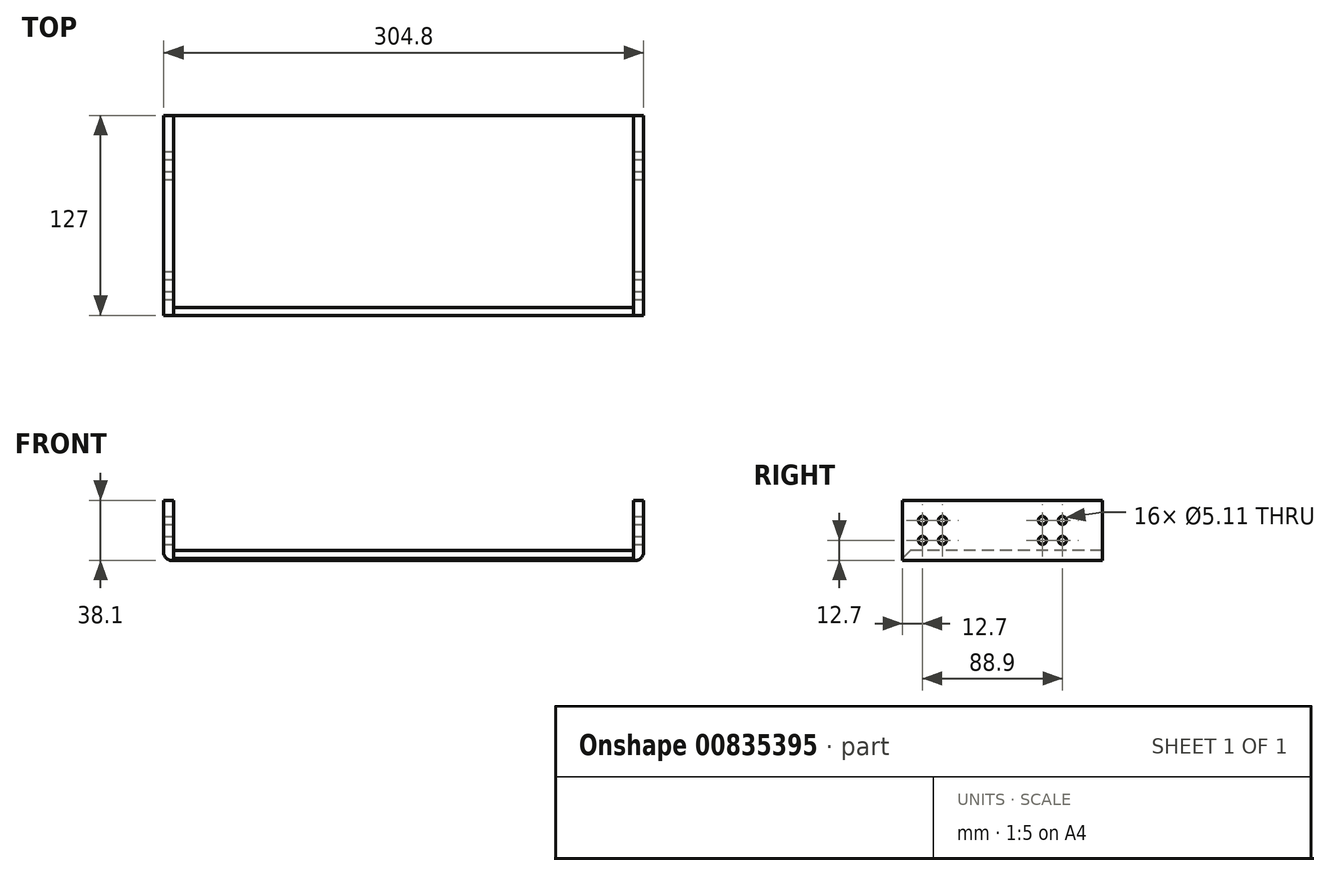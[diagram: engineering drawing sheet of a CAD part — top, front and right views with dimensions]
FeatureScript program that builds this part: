
annotation { "Feature Type Name" : "Feature", "Feature Type Description" : "" }
export const myFeature = defineFeature(function(context is Context, id is Id, definition is map)
    precondition{}
    {
        {
            var Q0;
            Q0=qCreatedBy(makeId("Front.planeOp"),FACE);
            var sketch = newSketch(context, id + "F0", { "sketchPlane" : qUnion([Q0])});
            skLineSegment(sketch, "E0.bottom", {"start": v(0, 0) * mm, "end": v(-304.8, 0) * mm});
            skLineSegment(sketch, "E0.top", {"start": v(0, 38.1) * mm, "end": v(-6.35, 38.1) * mm});
            skLineSegment(sketch, "E0.left", {"start": v(0, 0) * mm, "end": v(0, 38.1) * mm});
            skLineSegment(sketch, "E0.right", {"start": v(-304.8, 0) * mm, "end": v(-304.8, 38.1) * mm});
            skLineSegment(sketch, "E1.top", {"start": v(-304.8, 38.1) * mm, "end": v(-298.45, 38.1) * mm});
            skLineSegment(sketch, "E1.right", {"start": v(-298.45, 6.35) * mm, "end": v(-298.45, 38.1) * mm});
            skLineSegment(sketch, "E2.top", {"start": v(-298.45, 6.35) * mm, "end": v(-6.35, 6.35) * mm});
            skLineSegment(sketch, "E2.left", {"start": v(-298.45, 38.1) * mm, "end": v(-298.45, 6.35) * mm});
            skLineSegment(sketch, "E2.right", {"start": v(-6.35, 38.1) * mm, "end": v(-6.35, 6.35) * mm});
            skSolve(sketch);
        }
        {
            var Q0;
            Q0=makeQuery(id+"F0.imprint","IMPRINT",FACE,{"disambiguationData":[TD([[makeQuery(id+"F0.imprint","IMPRINT",EDGE,{"derivedFrom":sQuery(id+"F0.wireOp",EDGE,"E0.bottom")}),-1.0]])]});
            extrude(context, id + "F1", {"entities" : qUnion([Q0]), "oppositeDirection" : true, "depth" : 127 * mm, "offsetDistance" : 25.4 * mm});
        }
        {
            var Q0;
            Q0=makeQuery(id+"F1.opExtrude","SWEPT_EDGE",EDGE,{"disambiguationData":[OSD([sQuery(id+"F0.wireOp",EDGE,"E0.bottom"),sQuery(id+"F0.wireOp",EDGE,"E0.right")])]});
            var Q1;
            Q1=makeQuery(id+"F1.opExtrude","SWEPT_EDGE",EDGE,{"disambiguationData":[OSD([sQuery(id+"F0.wireOp",EDGE,"E0.bottom"),sQuery(id+"F0.wireOp",EDGE,"E0.left")])]});
            fillet(context, id + "F2", {"entities" : qUnion([Q0, Q1]), "radius" : 5.08 * mm, "tangentPropagation" : true, "allowEdgeOverflow" : false});
        }
        {
            var Q0;
            Q0=makeQuery(id+"F1.opExtrude","CAP_EDGE",EDGE,{"disambiguationData":[OSD([sQuery(id+"F0.wireOp",EDGE,"E2.top")])],"isStart":true});
            chamfer(context, id + "F3", {"entities" : qUnion([Q0]), "width" : 5.08 * mm});
        }
        {
            var Q0;
            Q0=qCreatedBy(makeId("Right.planeOp"),FACE);
            var sketch = newSketch(context, id + "F4", { "sketchPlane" : qUnion([Q0])});
            skLineSegment(sketch, "E3.bottom", {"start": v(0, 0) * mm, "end": v(12.7, 0) * mm});
            skCircle(sketch, "E4", {"center": v(12.7, 12.7) * mm, "radius": 2.55 * mm});
            skCircle(sketch, "E5", {"center": v(12.7, 25.4) * mm, "radius": 2.55 * mm});
            skCircle(sketch, "E6", {"center": v(25.4, 25.4) * mm, "radius": 2.55 * mm});
            skCircle(sketch, "E7", {"center": v(25.4, 12.7) * mm, "radius": 2.55 * mm});
            skCircle(sketch, "E8", {"center": v(88.9, 12.7) * mm, "radius": 2.55 * mm});
            skCircle(sketch, "E9", {"center": v(101.6, 12.7) * mm, "radius": 2.55 * mm});
            skCircle(sketch, "E10", {"center": v(101.6, 25.4) * mm, "radius": 2.55 * mm});
            skCircle(sketch, "E11", {"center": v(88.9, 25.4) * mm, "radius": 2.55 * mm});
            skSolve(sketch);
        }
        {
            var Q0;
            Q0 = qSketchRegion(id + "F4", true);
            extrude(context, id + "F5", {"entities" : qUnion([Q0]), "operationType" : NewBodyOperationType.REMOVE, "endBound" : BoundingType.THROUGH_ALL, "oppositeDirection" : true, "depth" : 25.4 * mm, "offsetDistance" : 25.4 * mm});
        }
    });
